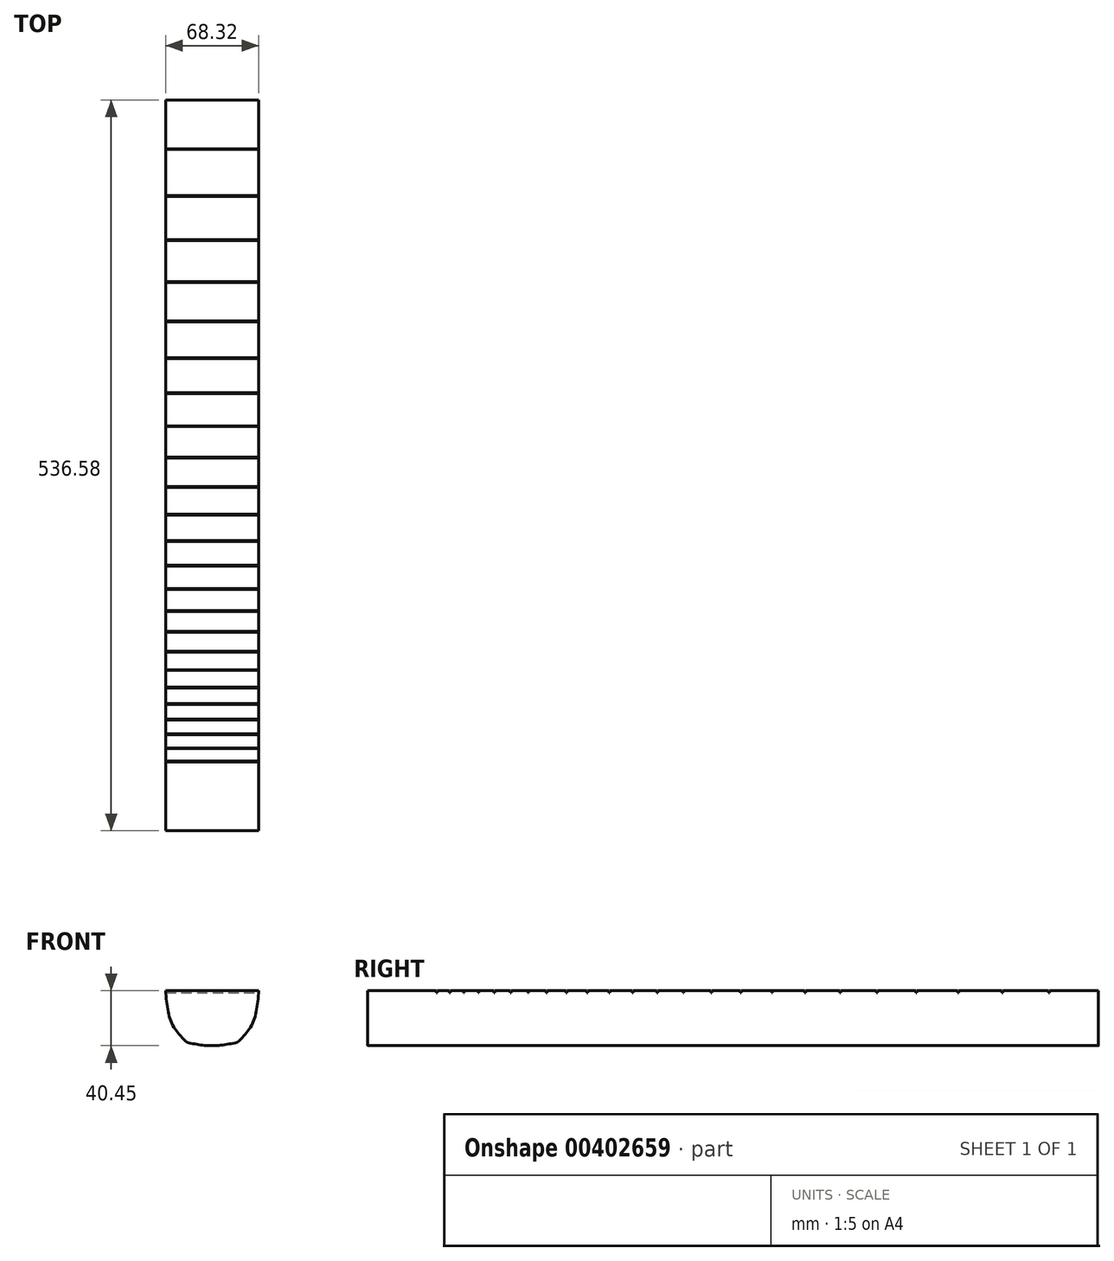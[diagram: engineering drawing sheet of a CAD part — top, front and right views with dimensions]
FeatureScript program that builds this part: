
annotation { "Feature Type Name" : "Feature", "Feature Type Description" : "" }
export const myFeature = defineFeature(function(context is Context, id is Id, definition is map)
    precondition{}
    {
        {
            var Q0;
            Q0=qCreatedBy(makeId("Front.planeOp"),FACE);
            var sketch = newSketch(context, id + "F0", { "sketchPlane" : qUnion([Q0])});
            skLineSegment(sketch, "E0.bottom", {"start": v(-34.16, 40.45) * mm, "end": v(34.16, 40.45) * mm});
            skFitSpline(sketch, "E1", {"points": [v(-34.16, 40.45) * mm, v(-29.87, 16.92) * mm, v(-18.6, 2.35) * mm], "startDerivative": vector(3.78, -47.66) * mm, "endDerivative": vector(27.89, -28.12) * mm});
            skFitSpline(sketch, "E2.MirrorCS", {"points": [v(34.16, 40.45) * mm, v(29.87, 16.92) * mm, v(18.6, 2.35) * mm], "startDerivative": vector(-3.78, -47.66) * mm, "endDerivative": vector(-27.89, -28.12) * mm});
            skFitSpline(sketch, "E3", {"points": [v(18.6, 2.35) * mm, v(-0.92, 0) * mm, v(-18.6, 2.35) * mm], "startDerivative": vector(-38.58, -7) * mm, "endDerivative": vector(-35.77, 7.12) * mm});
            skSolve(sketch);
        }
        {
            var Q0;
            Q0=qSketchRegion(id+"F0",true);
            var Q1;
            Q1=makeQuery(id+"F0.imprint","IMPRINT",FACE,{"disambiguationData":[TD([[makeQuery(id+"F0.imprint","IMPRINT",EDGE,{"derivedFrom":sQuery(id+"F0.wireOp",EDGE,"E0.bottom")}),-1.0]])]});
            extrude(context, id + "F1", {"entities" : qUnion([Q0, Q1]), "depth" : 647.7 * mm});
        }
        {
            var Q0;
            Q0=makeQuery(id+"F1.opExtrude","SWEPT_FACE",FACE,{"disambiguationData":[OSD([sQuery(id+"F0.wireOp",EDGE,"E0.bottom")])]});
            var sketch = newSketch(context, id + "F2", { "sketchPlane" : qUnion([Q0])});
            skLineSegment(sketch, "E4", {"start": v(-34.16, -536.58) * mm, "end": v(34.16, -536.58) * mm});
            skLineSegment(sketch, "E5", {"start": v(-34.16, -35.8) * mm, "end": v(34.16, -35.8) * mm});
            skLineSegment(sketch, "E6.MirrorCS", {"start": v(-34.16, -36.38) * mm, "end": v(34.16, -36.38) * mm});
            skLineSegment(sketch, "E7", {"start": v(-34.16, -70.14) * mm, "end": v(34.16, -70.14) * mm});
            skLineSegment(sketch, "E8.MirrorCS", {"start": v(-34.16, -70.72) * mm, "end": v(34.16, -70.72) * mm});
            skLineSegment(sketch, "E9", {"start": v(-34.16, -102.66) * mm, "end": v(34.16, -102.66) * mm});
            skLineSegment(sketch, "E10.MirrorCS", {"start": v(-34.16, -103.25) * mm, "end": v(34.16, -103.25) * mm});
            skLineSegment(sketch, "E11", {"start": v(-34.16, -133.36) * mm, "end": v(34.16, -133.36) * mm});
            skLineSegment(sketch, "E12.MirrorCS", {"start": v(-34.16, -133.94) * mm, "end": v(34.16, -133.94) * mm});
            skLineSegment(sketch, "E13", {"start": v(-34.16, -162.24) * mm, "end": v(34.16, -162.24) * mm});
            skLineSegment(sketch, "E14.MirrorCS", {"start": v(-34.16, -162.82) * mm, "end": v(34.16, -162.82) * mm});
            skLineSegment(sketch, "E15", {"start": v(-34.16, -189.35) * mm, "end": v(34.16, -189.35) * mm});
            skLineSegment(sketch, "E16.MirrorCS", {"start": v(-34.16, -189.93) * mm, "end": v(34.16, -189.93) * mm});
            skLineSegment(sketch, "E17", {"start": v(34.16, -215.03) * mm, "end": v(-34.16, -215.03) * mm});
            skLineSegment(sketch, "E18.MirrorCS", {"start": v(34.16, -215.62) * mm, "end": v(-34.16, -215.62) * mm});
            skLineSegment(sketch, "E19", {"start": v(-34.16, -239.28) * mm, "end": v(34.16, -239.28) * mm});
            skLineSegment(sketch, "E20.MirrorCS", {"start": v(-34.16, -239.86) * mm, "end": v(34.16, -239.86) * mm});
            skLineSegment(sketch, "E21", {"start": v(-34.16, -262.33) * mm, "end": v(34.16, -262.33) * mm});
            skLineSegment(sketch, "E22.MirrorCS", {"start": v(-34.16, -262.91) * mm, "end": v(34.16, -262.91) * mm});
            skLineSegment(sketch, "E23", {"start": v(34.16, -283.94) * mm, "end": v(-34.16, -283.94) * mm});
            skLineSegment(sketch, "E24.MirrorCS", {"start": v(34.16, -284.52) * mm, "end": v(-34.16, -284.52) * mm});
            skLineSegment(sketch, "E25", {"start": v(-34.16, -304.35) * mm, "end": v(34.16, -304.35) * mm});
            skLineSegment(sketch, "E26.MirrorCS", {"start": v(-34.16, -304.93) * mm, "end": v(34.16, -304.93) * mm});
            skLineSegment(sketch, "E27", {"start": v(-34.16, -323.56) * mm, "end": v(34.16, -323.56) * mm});
            skLineSegment(sketch, "E28.MirrorCS", {"start": v(-34.16, -324.14) * mm, "end": v(34.16, -324.14) * mm});
            skLineSegment(sketch, "E29", {"start": v(-34.16, -341.74) * mm, "end": v(34.16, -341.74) * mm});
            skLineSegment(sketch, "E30.MirrorCS", {"start": v(-34.16, -342.33) * mm, "end": v(34.16, -342.33) * mm});
            skLineSegment(sketch, "E31", {"start": v(-34.16, -358.9) * mm, "end": v(34.16, -358.9) * mm});
            skLineSegment(sketch, "E32.MirrorCS", {"start": v(-34.16, -359.48) * mm, "end": v(34.16, -359.48) * mm});
            skLineSegment(sketch, "E33", {"start": v(34.16, -375.04) * mm, "end": v(-34.16, -375.04) * mm});
            skLineSegment(sketch, "E34.MirrorCS", {"start": v(34.16, -375.62) * mm, "end": v(-34.16, -375.62) * mm});
            skLineSegment(sketch, "E35", {"start": v(-34.16, -390.38) * mm, "end": v(34.16, -390.38) * mm});
            skLineSegment(sketch, "E36.MirrorCS", {"start": v(-34.16, -390.97) * mm, "end": v(34.16, -390.97) * mm});
            skLineSegment(sketch, "E37", {"start": v(-34.16, -404.82) * mm, "end": v(34.16, -404.82) * mm});
            skLineSegment(sketch, "E38.MirrorCS", {"start": v(-34.16, -405.4) * mm, "end": v(34.16, -405.4) * mm});
            skLineSegment(sketch, "E39", {"start": v(-34.16, -418.38) * mm, "end": v(34.16, -418.38) * mm});
            skLineSegment(sketch, "E40.MirrorCS", {"start": v(-34.16, -418.96) * mm, "end": v(34.16, -418.96) * mm});
            skLineSegment(sketch, "E41", {"start": v(34.16, -431.25) * mm, "end": v(-34.16, -431.25) * mm});
            skLineSegment(sketch, "E42.MirrorCS", {"start": v(34.16, -431.84) * mm, "end": v(-34.16, -431.84) * mm});
            skLineSegment(sketch, "E43", {"start": v(-34.16, -443.4) * mm, "end": v(34.16, -443.4) * mm});
            skLineSegment(sketch, "E44.MirrorCS", {"start": v(-34.16, -443.98) * mm, "end": v(34.16, -443.98) * mm});
            skLineSegment(sketch, "E45", {"start": v(-34.16, -454.85) * mm, "end": v(34.16, -454.85) * mm});
            skLineSegment(sketch, "E46.MirrorCS", {"start": v(-34.16, -455.43) * mm, "end": v(34.16, -455.43) * mm});
            skLineSegment(sketch, "E47", {"start": v(-34.16, -465.65) * mm, "end": v(34.16, -465.65) * mm});
            skLineSegment(sketch, "E48.MirrorCS", {"start": v(-34.16, -466.23) * mm, "end": v(34.16, -466.23) * mm});
            skLineSegment(sketch, "E49", {"start": v(-34.16, -475.86) * mm, "end": v(34.16, -475.86) * mm});
            skLineSegment(sketch, "E50.MirrorCS", {"start": v(-34.16, -476.44) * mm, "end": v(34.16, -476.44) * mm});
            skLineSegment(sketch, "E51", {"start": v(-34.16, -485.48) * mm, "end": v(34.16, -485.48) * mm});
            skLineSegment(sketch, "E52.MirrorCS", {"start": v(-34.16, -486.07) * mm, "end": v(34.16, -486.07) * mm});
            skSolve(sketch);
        }
        {
            var Q0;
            {var subQ0=sQuery(id+"F2.wireOp",EDGE,"E4");Q0=makeQuery(id+"F2.imprint","IMPRINT",FACE,{"disambiguationData":[TD([[makeQuery(id+"F2.imprint","IMPRINT",EDGE,{"derivedFrom":subQ0}),-1.0]])]});}
            extrude(context, id + "F3", {"entities" : qUnion([Q0]), "operationType" : NewBodyOperationType.REMOVE, "oppositeDirection" : true, "depth" : 76.2 * mm, "hasSecondDirection" : true, "secondDirectionOppositeDirection" : false, "secondDirectionDepth" : 25.4 * mm});
        }
        {
            var Q0;
            {var subQ0=sQuery(id+"F2.wireOp",EDGE,"E5");Q0=makeQuery(id+"F2.imprint","IMPRINT",FACE,{"disambiguationData":[TD([[makeQuery(id+"F2.imprint","IMPRINT",EDGE,{"derivedFrom":subQ0}),-1.0]])]});}
            var Q1;
            {var subQ0=sQuery(id+"F2.wireOp",EDGE,"E7");Q1=makeQuery(id+"F2.imprint","IMPRINT",FACE,{"disambiguationData":[TD([[makeQuery(id+"F2.imprint","IMPRINT",EDGE,{"derivedFrom":subQ0}),-1.0]])]});}
            var Q2;
            {var subQ0=sQuery(id+"F2.wireOp",EDGE,"E9");Q2=makeQuery(id+"F2.imprint","IMPRINT",FACE,{"disambiguationData":[TD([[makeQuery(id+"F2.imprint","IMPRINT",EDGE,{"derivedFrom":subQ0}),-1.0]])]});}
            var Q3;
            {var subQ0=sQuery(id+"F2.wireOp",EDGE,"E11");Q3=makeQuery(id+"F2.imprint","IMPRINT",FACE,{"disambiguationData":[TD([[makeQuery(id+"F2.imprint","IMPRINT",EDGE,{"derivedFrom":subQ0}),-1.0]])]});}
            var Q4;
            {var subQ0=sQuery(id+"F2.wireOp",EDGE,"E13");Q4=makeQuery(id+"F2.imprint","IMPRINT",FACE,{"disambiguationData":[TD([[makeQuery(id+"F2.imprint","IMPRINT",EDGE,{"derivedFrom":subQ0}),-1.0]])]});}
            var Q5;
            {var subQ0=sQuery(id+"F2.wireOp",EDGE,"E15");Q5=makeQuery(id+"F2.imprint","IMPRINT",FACE,{"disambiguationData":[TD([[makeQuery(id+"F2.imprint","IMPRINT",EDGE,{"derivedFrom":subQ0}),-1.0]])]});}
            var Q6;
            {var subQ0=sQuery(id+"F2.wireOp",EDGE,"E17");Q6=makeQuery(id+"F2.imprint","IMPRINT",FACE,{"disambiguationData":[TD([[makeQuery(id+"F2.imprint","IMPRINT",EDGE,{"derivedFrom":subQ0}),1.0]])]});}
            var Q7;
            {var subQ0=sQuery(id+"F2.wireOp",EDGE,"E19");Q7=makeQuery(id+"F2.imprint","IMPRINT",FACE,{"disambiguationData":[TD([[makeQuery(id+"F2.imprint","IMPRINT",EDGE,{"derivedFrom":subQ0}),-1.0]])]});}
            var Q8;
            {var subQ0=sQuery(id+"F2.wireOp",EDGE,"E21");Q8=makeQuery(id+"F2.imprint","IMPRINT",FACE,{"disambiguationData":[TD([[makeQuery(id+"F2.imprint","IMPRINT",EDGE,{"derivedFrom":subQ0}),-1.0]])]});}
            var Q9;
            {var subQ0=sQuery(id+"F2.wireOp",EDGE,"E23");Q9=makeQuery(id+"F2.imprint","IMPRINT",FACE,{"disambiguationData":[TD([[makeQuery(id+"F2.imprint","IMPRINT",EDGE,{"derivedFrom":subQ0}),1.0]])]});}
            var Q10;
            {var subQ0=sQuery(id+"F2.wireOp",EDGE,"E25");Q10=makeQuery(id+"F2.imprint","IMPRINT",FACE,{"disambiguationData":[TD([[makeQuery(id+"F2.imprint","IMPRINT",EDGE,{"derivedFrom":subQ0}),-1.0]])]});}
            var Q11;
            {var subQ0=sQuery(id+"F2.wireOp",EDGE,"E27");Q11=makeQuery(id+"F2.imprint","IMPRINT",FACE,{"disambiguationData":[TD([[makeQuery(id+"F2.imprint","IMPRINT",EDGE,{"derivedFrom":subQ0}),-1.0]])]});}
            var Q12;
            {var subQ0=sQuery(id+"F2.wireOp",EDGE,"E29");Q12=makeQuery(id+"F2.imprint","IMPRINT",FACE,{"disambiguationData":[TD([[makeQuery(id+"F2.imprint","IMPRINT",EDGE,{"derivedFrom":subQ0}),-1.0]])]});}
            var Q13;
            {var subQ0=sQuery(id+"F2.wireOp",EDGE,"E31");Q13=makeQuery(id+"F2.imprint","IMPRINT",FACE,{"disambiguationData":[TD([[makeQuery(id+"F2.imprint","IMPRINT",EDGE,{"derivedFrom":subQ0}),-1.0]])]});}
            var Q14;
            {var subQ0=sQuery(id+"F2.wireOp",EDGE,"E33");Q14=makeQuery(id+"F2.imprint","IMPRINT",FACE,{"disambiguationData":[TD([[makeQuery(id+"F2.imprint","IMPRINT",EDGE,{"derivedFrom":subQ0}),1.0]])]});}
            var Q15;
            {var subQ0=sQuery(id+"F2.wireOp",EDGE,"E35");Q15=makeQuery(id+"F2.imprint","IMPRINT",FACE,{"disambiguationData":[TD([[makeQuery(id+"F2.imprint","IMPRINT",EDGE,{"derivedFrom":subQ0}),-1.0]])]});}
            var Q16;
            {var subQ0=sQuery(id+"F2.wireOp",EDGE,"E37");Q16=makeQuery(id+"F2.imprint","IMPRINT",FACE,{"disambiguationData":[TD([[makeQuery(id+"F2.imprint","IMPRINT",EDGE,{"derivedFrom":subQ0}),-1.0]])]});}
            var Q17;
            {var subQ0=sQuery(id+"F2.wireOp",EDGE,"E39");Q17=makeQuery(id+"F2.imprint","IMPRINT",FACE,{"disambiguationData":[TD([[makeQuery(id+"F2.imprint","IMPRINT",EDGE,{"derivedFrom":subQ0}),-1.0]])]});}
            var Q18;
            {var subQ0=sQuery(id+"F2.wireOp",EDGE,"E41");Q18=makeQuery(id+"F2.imprint","IMPRINT",FACE,{"disambiguationData":[TD([[makeQuery(id+"F2.imprint","IMPRINT",EDGE,{"derivedFrom":subQ0}),1.0]])]});}
            var Q19;
            {var subQ0=sQuery(id+"F2.wireOp",EDGE,"E43");Q19=makeQuery(id+"F2.imprint","IMPRINT",FACE,{"disambiguationData":[TD([[makeQuery(id+"F2.imprint","IMPRINT",EDGE,{"derivedFrom":subQ0}),-1.0]])]});}
            var Q20;
            {var subQ0=sQuery(id+"F2.wireOp",EDGE,"E45");Q20=makeQuery(id+"F2.imprint","IMPRINT",FACE,{"disambiguationData":[TD([[makeQuery(id+"F2.imprint","IMPRINT",EDGE,{"derivedFrom":subQ0}),-1.0]])]});}
            var Q21;
            {var subQ0=sQuery(id+"F2.wireOp",EDGE,"E47");Q21=makeQuery(id+"F2.imprint","IMPRINT",FACE,{"disambiguationData":[TD([[makeQuery(id+"F2.imprint","IMPRINT",EDGE,{"derivedFrom":subQ0}),-1.0]])]});}
            var Q22;
            {var subQ0=sQuery(id+"F2.wireOp",EDGE,"E49");Q22=makeQuery(id+"F2.imprint","IMPRINT",FACE,{"disambiguationData":[TD([[makeQuery(id+"F2.imprint","IMPRINT",EDGE,{"derivedFrom":subQ0}),-1.0]])]});}
            var Q23;
            {var subQ0=sQuery(id+"F2.wireOp",EDGE,"E51");Q23=makeQuery(id+"F2.imprint","IMPRINT",FACE,{"disambiguationData":[TD([[makeQuery(id+"F2.imprint","IMPRINT",EDGE,{"derivedFrom":subQ0}),-1.0]])]});}
            extrude(context, id + "F4", {"entities" : qUnion([Q0, Q1, Q2, Q3, Q4, Q5, Q6, Q7, Q8, Q9, Q10, Q11, Q12, Q13, Q14, Q15, Q16, Q17, Q18, Q19, Q20, Q21, Q22, Q23]), "operationType" : NewBodyOperationType.REMOVE, "oppositeDirection" : true, "depth" : 1.45 * mm});
        }
        {
            var Q0;
            Q0=makeQuery(id+"F1.opExtrude","SWEPT_EDGE",EDGE,{"disambiguationData":[OSD([sQuery(id+"F0.wireOp",EDGE,"E1"),sQuery(id+"F0.wireOp",EDGE,"E3")])]});
            fillet(context, id + "F5", {"entities" : qUnion([Q0]), "radius" : 5.08 * mm, "tangentPropagation" : true, "allowEdgeOverflow" : false});
        }
        {
            var Q0;
            Q0=makeQuery(id+"F1.opExtrude","SWEPT_EDGE",EDGE,{"disambiguationData":[OSD([sQuery(id+"F0.wireOp",EDGE,"E2.MirrorCS"),sQuery(id+"F0.wireOp",EDGE,"E3")])]});
            fillet(context, id + "F6", {"entities" : qUnion([Q0]), "radius" : 5.08 * mm, "tangentPropagation" : true, "allowEdgeOverflow" : false});
        }
    });
